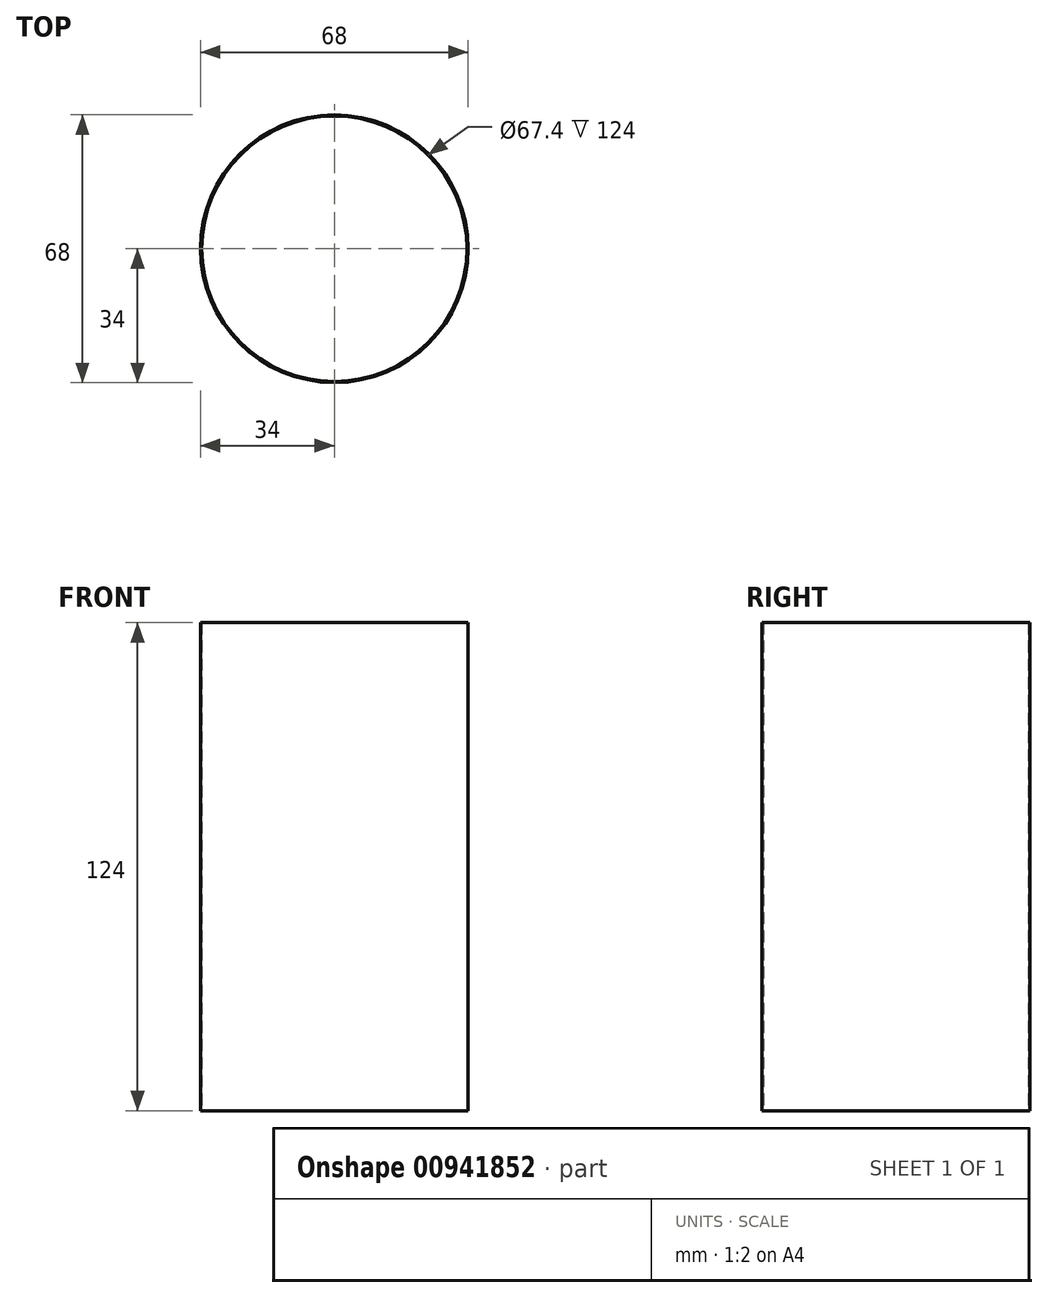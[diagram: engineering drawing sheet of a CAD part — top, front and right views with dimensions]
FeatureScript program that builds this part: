
annotation { "Feature Type Name" : "Feature", "Feature Type Description" : "" }
export const myFeature = defineFeature(function(context is Context, id is Id, definition is map)
    precondition{}
    {
        {
            var Q0;
            Q0=qCreatedBy(makeId("Top.planeOp"),FACE);
            var sketch = newSketch(context, id + "F0", { "sketchPlane" : qUnion([Q0])});
            skCircle(sketch, "E0", {"center": v(0, 0) * mm, "radius": 34 * mm});
            skCircle(sketch, "E1.0", {"center": v(0, 0) * mm, "radius": 33.7 * mm});
            skSolve(sketch);
        }
        {
            var Q0;
            Q0 = qSketchRegion(id + "F0", true);
            extrude(context, id + "F1", {"entities" : qUnion([Q0]), "depth" : 62 * mm, "offsetDistance" : 25.4 * mm, "hasSecondDirection" : true, "secondDirectionOppositeDirection" : true, "secondDirectionDepth" : 62 * mm});
        }
    });
